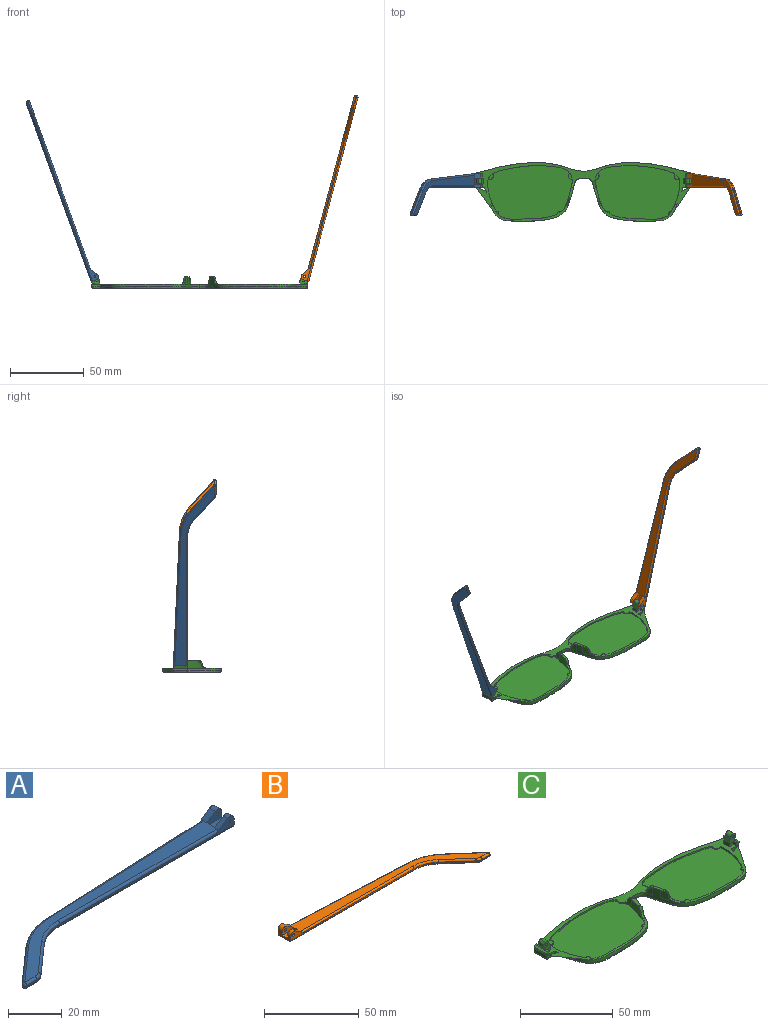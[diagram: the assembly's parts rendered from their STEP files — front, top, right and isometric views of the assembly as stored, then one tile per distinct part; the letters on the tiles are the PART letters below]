
ASSEMBLY  parts=3 mates=2
PART A: 43 faces, bbox 130.2x29.5x5.9 mm
  f0: plane 9.62x3.72mm, normal (1,0,0), area 24.7mm2, adj f1,f3,f4,f5,f10,f16,f18,f28
  f1: cylinder r=2.2mm len=3.45mm, axis (0,-1,0), area 11mm2, adj f0,f2,f4,f37
  f2: plane 6.01x3.91mm, normal (-0.55,0,0.84), area 12.7mm2, adj f1,f4,f9,f19,f37
  f3: plane 2.26x0.1mm, normal (0,0,1), area 0.1mm2, adj f0,f5,f18
  f4: plane 92.1x4.9mm, normal (0,-1,0), area 79.9mm2, adj f0,f1,f2,f14,f19,f36,f42
  f5: plane 93.42x4.13mm, normal (-0.04,1,0), area 64.8mm2, adj f0,f3,f11,f15,f17,f27,f28
  f6: plane 17.82x15.72mm, normal (-0.66,0.75,0), area 14.3mm2, adj f11,f12,f25,f30
  f7: plane 5.46x0.6mm, normal (0,-1,0), area 3.3mm2, adj f12,f13,f23,f32
  f8: plane 14.99x13.23mm, normal (0.66,-0.75,0), area 12mm2, adj f13,f14,f21,f34
  f9: plane 121.18x26.73mm, normal (0,0,1), area 627.7mm2, adj f2,f17,f19,f20,f21,f22,f23,f25
  f10: plane 129.1x27.08mm, normal (0,0,-1), area 686.5mm2, adj f0,f28,f29,f30,f32,f33,f34,f35
  f11: cylinder r=30mm len=18.52mm, axis (0,0,-1), area 12.2mm2, adj f5,f6,f26,f29
  f12: cylinder r=1mm len=1.75mm, axis (0,0,-1), area 1.5mm2, adj f6,f7,f24,f31
  f13: cylinder r=5mm len=3.31mm, axis (0,0,-1), area 2.2mm2, adj f7,f8,f22,f33
  f14: cylinder r=20mm len=13.23mm, axis (0,0,1), area 8.7mm2, adj f4,f8,f20,f35
  f15: plane 5.66x0.25mm, normal (0,0,-1), area 0.7mm2, adj f5,f17,f18
  f16: cylinder r=2.2mm len=3.45mm, axis (0,-1,0), area 14.8mm2, adj f0,f17,f18,f38
  f17: plane 6.01x3.91mm, normal (-0.55,0,0.84), area 16.9mm2, adj f5,f9,f15,f16,f18,f27,f38
  f18: plane 7.92x3.3mm, normal (0,1,0), area 15.9mm2, adj f0,f3,f15,f16,f17,f41
  f19: cylinder r=1mm len=84.18mm, axis (-1,0,0), area 131.4mm2, adj f2,f4,f9,f20
  f20: torus R=21mm, axis (0,0,1), area 23.1mm2, adj f9,f14,f19,f21
  f21: cylinder r=1mm len=15.65mm, axis (-0.75,-0.66,0), area 31.4mm2, adj f8,f9,f20,f22
  f22: torus R=4mm, axis (0,0,1), area 5.3mm2, adj f9,f13,f21,f23
  f23: cylinder r=1mm len=5.46mm, axis (-1,0,0), area 8.6mm2, adj f7,f9,f22,f24
  f24: sphere r=1mm, area 2.4mm2, adj f12,f23,f25
  f25: cylinder r=1mm len=18.48mm, axis (0.75,0.66,0), area 37.3mm2, adj f6,f9,f24,f26
  f26: torus R=29mm, axis (0,0,1), area 31.6mm2, adj f9,f11,f25,f27
  f27: cylinder r=1mm len=85.5mm, axis (1,0.04,0), area 133.5mm2, adj f5,f9,f17,f26
  f28: cylinder r=1mm len=93.46mm, axis (-1,-0.04,0), area 146.9mm2, adj f0,f5,f10,f29
  f29: torus R=29mm, axis (0,0,1), area 31.6mm2, adj f10,f11,f28,f30
  f30: cylinder r=1mm len=18.48mm, axis (-0.75,-0.66,0), area 37.3mm2, adj f6,f10,f29,f31
  f31: sphere r=1mm, area 2.4mm2, adj f12,f30,f32
  f32: cylinder r=1mm len=5.46mm, axis (1,0,0), area 8.6mm2, adj f7,f10,f31,f33
  f33: torus R=4mm, axis (0,0,1), area 5.3mm2, adj f10,f13,f32,f34
  f34: cylinder r=1mm len=15.65mm, axis (0.75,0.66,0), area 31.4mm2, adj f8,f10,f33,f35
  f35: torus R=21mm, axis (0,0,1), area 23.1mm2, adj f10,f14,f34,f36
  f36: cylinder r=1mm len=92.1mm, axis (1,0,0), area 144.7mm2, adj f0,f4,f10,f35
  f37: plane 7.92x4.7mm, normal (0,1,0), area 27mm2, adj f0,f1,f2,f39,f40,f42
  f38: plane 7.92x4.7mm, normal (0,-1,0), area 27mm2, adj f0,f16,f17,f39,f40,f41
  f39: plane 7.92x4.1mm, normal (0,0,1), area 32.5mm2, adj f0,f37,f38,f40
  f40: plane 4.1x1.4mm, normal (1,0,0), area 5.7mm2, adj f9,f37,f38,f39
  f41: cylinder r=0.5mm len=3.1mm, axis (0,-1,0), area 9.7mm2, adj f18,f38
  f42: cylinder r=0.5mm len=2.3mm, axis (0,-1,0), area 7.2mm2, adj f4,f37
PART B: 43 faces, bbox 130.2x29.5x5.9 mm
  f0: plane 9.62x3.72mm, normal (-1,0,0), area 24.7mm2, adj f1,f3,f4,f5,f10,f16,f18,f28
  f1: cylinder r=2.2mm len=3.45mm, axis (0,-1,0), area 11mm2, adj f0,f2,f4,f37
  f2: plane 6.01x3.91mm, normal (0.55,0,0.84), area 12.7mm2, adj f1,f4,f9,f19,f37
  f3: plane 2.26x0.1mm, normal (0,0,1), area 0.1mm2, adj f0,f5,f18
  f4: plane 92.1x4.9mm, normal (0,-1,0), area 78.2mm2, adj f0,f1,f2,f14,f19,f36,f42
  f5: plane 93.42x4.13mm, normal (0.04,1,0), area 64.8mm2, adj f0,f3,f11,f15,f17,f27,f28
  f6: plane 17.82x15.72mm, normal (0.66,0.75,0), area 14.3mm2, adj f11,f12,f25,f30
  f7: plane 5.46x0.6mm, normal (0,-1,0), area 3.3mm2, adj f12,f13,f23,f32
  f8: plane 14.99x13.23mm, normal (-0.66,-0.75,0), area 12mm2, adj f13,f14,f21,f34
  f9: plane 121.18x26.73mm, normal (0,0,1), area 627.7mm2, adj f2,f17,f19,f20,f21,f22,f23,f25
  f10: plane 129.1x27.08mm, normal (0,0,-1), area 686.5mm2, adj f0,f28,f29,f30,f32,f33,f34,f35
  f11: cylinder r=30mm len=18.52mm, axis (0,0,-1), area 12.2mm2, adj f5,f6,f26,f29
  f12: cylinder r=1mm len=1.75mm, axis (0,0,-1), area 1.5mm2, adj f6,f7,f24,f31
  f13: cylinder r=5mm len=3.31mm, axis (0,0,-1), area 2.2mm2, adj f7,f8,f22,f33
  f14: cylinder r=20mm len=13.23mm, axis (0,0,1), area 8.7mm2, adj f4,f8,f20,f35
  f15: plane 5.66x0.25mm, normal (0,0,-1), area 0.7mm2, adj f5,f17,f18
  f16: cylinder r=2.2mm len=3.45mm, axis (0,-1,0), area 14.8mm2, adj f0,f17,f18,f38
  f17: plane 6.01x3.91mm, normal (0.55,0,0.84), area 16.9mm2, adj f5,f9,f15,f16,f18,f27,f38
  f18: plane 7.92x3.3mm, normal (0,1,0), area 14.3mm2, adj f0,f3,f15,f16,f17,f41
  f19: cylinder r=1mm len=84.18mm, axis (1,0,0), area 131.4mm2, adj f2,f4,f9,f20
  f20: torus R=21mm, axis (0,0,1), area 23.1mm2, adj f9,f14,f19,f21
  f21: cylinder r=1mm len=15.65mm, axis (0.75,-0.66,0), area 31.4mm2, adj f8,f9,f20,f22
  f22: torus R=4mm, axis (0,0,1), area 5.3mm2, adj f9,f13,f21,f23
  f23: cylinder r=1mm len=5.46mm, axis (1,0,0), area 8.6mm2, adj f7,f9,f22,f24
  f24: sphere r=1mm, area 2.4mm2, adj f12,f23,f25
  f25: cylinder r=1mm len=18.48mm, axis (-0.75,0.66,0), area 37.3mm2, adj f6,f9,f24,f26
  f26: torus R=29mm, axis (0,0,1), area 31.6mm2, adj f9,f11,f25,f27
  f27: cylinder r=1mm len=85.5mm, axis (-1,0.04,0), area 133.5mm2, adj f5,f9,f17,f26
  f28: cylinder r=1mm len=93.46mm, axis (1,-0.04,0), area 146.9mm2, adj f0,f5,f10,f29
  f29: torus R=29mm, axis (0,0,1), area 31.6mm2, adj f10,f11,f28,f30
  f30: cylinder r=1mm len=18.48mm, axis (0.75,-0.66,0), area 37.3mm2, adj f6,f10,f29,f31
  f31: sphere r=1mm, area 2.4mm2, adj f12,f30,f32
  f32: cylinder r=1mm len=5.46mm, axis (-1,0,0), area 8.6mm2, adj f7,f10,f31,f33
  f33: torus R=4mm, axis (0,0,1), area 5.3mm2, adj f10,f13,f32,f34
  f34: cylinder r=1mm len=15.65mm, axis (-0.75,0.66,0), area 31.4mm2, adj f8,f10,f33,f35
  f35: torus R=21mm, axis (0,0,1), area 23.1mm2, adj f10,f14,f34,f36
  f36: cylinder r=1mm len=92.1mm, axis (-1,0,0), area 144.7mm2, adj f0,f4,f10,f35
  f37: plane 7.92x4.7mm, normal (0,1,0), area 25.4mm2, adj f0,f1,f2,f39,f40,f42
  f38: plane 7.92x4.7mm, normal (0,-1,0), area 25.4mm2, adj f0,f16,f17,f39,f40,f41
  f39: plane 7.92x4.1mm, normal (0,0,1), area 32.5mm2, adj f0,f37,f38,f40
  f40: plane 4.1x1.4mm, normal (-1,0,0), area 5.7mm2, adj f9,f37,f38,f39
  f41: cylinder r=0.88mm len=3.1mm, axis (0,-1,0), area 17mm2, adj f18,f38
  f42: cylinder r=0.88mm len=2.3mm, axis (0,-1,0), area 12.6mm2, adj f4,f37
PART C: 104 faces, bbox 148.3x41x18.1 mm
  f0: plane 4.6x0.78mm, normal (0,0,1), area 0.1mm2, adj f10,f39
  f1: plane 147.86x40.62mm, normal (0,0,1), area 720.8mm2, adj f3,f4,f5,f6,f7,f10,f20,f23
  f2: plane 4.67x1.52mm, normal (0,0,1), area 0.1mm2, adj f6,f38
  f3: plane 1.23x0.04mm, normal (0,0,1), area 0mm2, adj f1,f6,f22
  f4: plane 6.97x5.07mm, normal (0,1,0), area 22.7mm2, adj f1,f20,f21,f25,f27,f28,f30,f31
  f5: plane 3.2x2.36mm, normal (0,-1,0), area 5.7mm2, adj f1,f20,f26,f29
  f6: extruded ~73.26x39.84mm, area 294.3mm2, adj f1,f2,f3,f7,f11,f13,f14,f15
  f7: extruded ~35.39x5.69mm, area 72.2mm2, adj f1,f6,f18,f59
  f8: plane 144.78x37.85mm, normal (0,0,-1), area 582.4mm2, adj f13,f15,f17,f18,f19,f64,f66,f68
  f9: plane 54.45x34.13mm, normal (0,0,-1), area 1549.9mm2, adj f19
  f10: extruded ~57.29x36.52mm, area 218.9mm2, adj f0,f1,f12,f39,f40,f42,f43,f44
  f11: plane 3.75x1.08mm, normal (0,0,1), area 0.1mm2, adj f6,f37
  f12: plane 57.58x36.73mm, normal (0,0,1), area 1771.7mm2, adj f10
  f13: bspline ~73.27x30.39mm, area 161.7mm2, adj f6,f8,f14,f64
  f14: bspline ~1x1mm, area 0.8mm2, adj f6,f13,f15
  f15: bspline ~8.99x1.23mm, area 12.6mm2, adj f6,f8,f14,f16
  f16: bspline ~1.04x1mm, area 0.7mm2, adj f6,f15,f17
  f17: bspline ~45.86x8.59mm, area 59.8mm2, adj f6,f8,f16,f18
  f18: bspline ~37.01x6.7mm, area 56.6mm2, adj f7,f8,f17,f69
  f19: bspline ~56.23x35.9mm, area 235.3mm2, adj f8,f9
  f20: plane 4x2.36mm, normal (-1,0,0), area 9.5mm2, adj f1,f4,f5,f21
  f21: plane 4x0.02mm, normal (0.34,0,0.94), area 0.1mm2, adj f4,f20,f28
  f22: plane 2.76x2.53mm, normal (0,-1,0), area 3.9mm2, adj f3,f26,f27,f35,f52
  f23: plane 7.67x1.6mm, normal (0.94,0,-0.34), area 13mm2, adj f1,f35,f36,f52
  f24: plane 2.1x1.69mm, normal (0,1,0), area 2.8mm2, adj f1,f25,f27,f36,f52
  f25: plane 3.3x2.1mm, normal (-1,0,0), area 6.9mm2, adj f1,f4,f24,f27
  f26: plane 2.35x2.1mm, normal (-1,0,0), area 4.9mm2, adj f1,f5,f22,f27,f29
  f27: plane 9.65x1.24mm, normal (0,0,1), area 8.2mm2, adj f4,f22,f24,f25,f26,f29,f30,f52
  f28: plane 4x3.31mm, normal (-0.94,0,0.34), area 14.1mm2, adj f4,f21,f29,f32
  f29: plane 5.77x5.06mm, normal (0,-1,0), area 17mm2, adj f5,f26,f27,f28,f30,f31,f32,f33
  f30: plane 4x2.21mm, normal (0.94,0,-0.34), area 9.4mm2, adj f4,f27,f29,f33
  f31: plane 4x0.01mm, normal (0.34,0,0.94), area 0mm2, adj f4,f29,f32,f33
  f32: cylinder r=1.98mm len=4mm, axis (0,1,0), area 12.4mm2, adj f4,f28,f29,f31
  f33: cylinder r=1.98mm len=4mm, axis (0,-1,0), area 12.4mm2, adj f4,f29,f30,f31
  f34: cylinder r=0.88mm len=4mm, axis (0,-1,0), area 22mm2, adj f4,f29
  f35: cone r=1mm half-angle=20deg, axis (0,0,1), area 2.3mm2, adj f1,f22,f23,f52
  f36: cylinder r=1mm len=2.28mm, axis (-0.34,0,-0.94), area 3mm2, adj f1,f23,f24,f52
  f37: extruded ~4.92x3.67mm, area 11.8mm2, adj f6,f11,f41
  f38: extruded ~5x4.64mm, area 23.3mm2, adj f2,f6,f40,f42,f51
  f39: extruded ~5x4.5mm, area 17.5mm2, adj f0,f10,f40,f41
  f40: plane 8.99x2.94mm, normal (0,0,1), area 10.5mm2, adj f6,f10,f38,f39,f41,f42
  f41: bspline ~15.56x15.29mm, area 14.1mm2, adj f1,f6,f37,f39,f40
  f42: bspline ~7.27x7.27mm, area 6.2mm2, adj f10,f38,f40,f51
  f43: plane 4.19x2.6mm, normal (0,0,-1), area 6.8mm2, adj f10,f44
  f44: cylinder r=2.28mm len=4.15mm, axis (0,0,1), area 3mm2, adj f1,f10,f43
  f45: plane 3.78x3.41mm, normal (0,0,-1), area 7.2mm2, adj f10,f46
  f46: cylinder r=2.28mm len=3.76mm, axis (0,0,1), area 3.2mm2, adj f1,f10,f45
  f47: plane 2.35x1.81mm, normal (0,0,-1), area 2.3mm2, adj f10,f48
  f48: cylinder r=1.3mm len=2.35mm, axis (0,0,1), area 1.9mm2, adj f1,f10,f47
  f49: plane 2.19x1.79mm, normal (0,0,-1), area 2mm2, adj f10,f50
  f50: cylinder r=1.3mm len=2.18mm, axis (0,0,1), area 1.7mm2, adj f1,f10,f49
  f51: bspline ~3.71x3.51mm, area 5.7mm2, adj f1,f6,f10,f38,f42
  f52: plane 9.71x1.44mm, normal (0.34,0,0.94), area 13.9mm2, adj f22,f23,f24,f27,f35,f36
  f53: plane 4.6x0.78mm, normal (0,0,1), area 0.1mm2, adj f61,f90
  f54: plane 4.67x1.52mm, normal (0,0,1), area 0.1mm2, adj f58,f89
  f55: plane 1.23x0.04mm, normal (0,0,1), area 0mm2, adj f1,f58,f73
  f56: plane 6.97x5.07mm, normal (0,1,0), area 22.7mm2, adj f1,f71,f72,f76,f78,f79,f81,f82
  f57: plane 3.2x2.36mm, normal (0,-1,0), area 5.7mm2, adj f1,f71,f77,f80
  f58: extruded ~73.26x39.84mm, area 294.3mm2, adj f1,f6,f54,f55,f59,f62,f64,f65
  f59: extruded ~35.39x5.69mm, area 72.2mm2, adj f1,f7,f58,f69
  f60: plane 54.45x34.13mm, normal (0,0,-1), area 1549.9mm2, adj f70
  f61: extruded ~57.29x36.52mm, area 219mm2, adj f1,f53,f63,f90,f91,f93,f94,f95
  f62: plane 3.75x1.08mm, normal (0,0,1), area 0.1mm2, adj f58,f88
  f63: plane 57.58x36.73mm, normal (0,0,1), area 1771.7mm2, adj f61
  f64: bspline ~73.83x30.39mm, area 161.7mm2, adj f8,f13,f58,f65
  f65: bspline ~1x1mm, area 0.8mm2, adj f58,f64,f66
  f66: bspline ~8.99x1.23mm, area 12.6mm2, adj f8,f58,f65,f67
  f67: bspline ~1.04x1mm, area 0.8mm2, adj f58,f66,f68
  f68: bspline ~45.86x8.59mm, area 59.8mm2, adj f8,f58,f67,f69
  f69: bspline ~37.01x6.7mm, area 56.6mm2, adj f8,f18,f59,f68
  f70: bspline ~56.22x35.9mm, area 235.3mm2, adj f8,f60
  f71: plane 4x2.36mm, normal (1,0,0), area 9.5mm2, adj f1,f56,f57,f72
  f72: plane 4x0.02mm, normal (-0.34,0,0.94), area 0.1mm2, adj f56,f71,f79
  f73: plane 2.76x2.53mm, normal (0,-1,0), area 3.9mm2, adj f55,f77,f78,f86,f103
  f74: plane 7.67x1.6mm, normal (-0.94,0,-0.34), area 13mm2, adj f1,f86,f87,f103
  f75: plane 2.1x1.69mm, normal (0,1,0), area 2.8mm2, adj f1,f76,f78,f87,f103
  f76: plane 3.3x2.1mm, normal (1,0,0), area 6.9mm2, adj f1,f56,f75,f78
  f77: plane 2.35x2.1mm, normal (1,0,0), area 4.9mm2, adj f1,f57,f73,f78,f80
  f78: plane 9.65x1.24mm, normal (0,0,1), area 8.2mm2, adj f56,f73,f75,f76,f77,f80,f81,f103
  f79: plane 4x3.31mm, normal (0.94,0,0.34), area 14.1mm2, adj f56,f72,f80,f83
  f80: plane 5.77x5.06mm, normal (0,-1,0), area 17mm2, adj f57,f77,f78,f79,f81,f82,f83,f84
  f81: plane 4x2.21mm, normal (-0.94,0,-0.34), area 9.4mm2, adj f56,f78,f80,f84
  f82: plane 4x0.01mm, normal (-0.34,0,0.94), area 0mm2, adj f56,f80,f83,f84
  f83: cylinder r=1.98mm len=4mm, axis (0,1,0), area 12.4mm2, adj f56,f79,f80,f82
  f84: cylinder r=1.98mm len=4mm, axis (0,-1,0), area 12.4mm2, adj f56,f80,f81,f82
  f85: cylinder r=0.88mm len=4mm, axis (0,-1,0), area 22mm2, adj f56,f80
  f86: cone r=1mm half-angle=20deg, axis (0,0,1), area 2.3mm2, adj f1,f73,f74,f103
  f87: cylinder r=1mm len=2.28mm, axis (0.34,0,-0.94), area 3mm2, adj f1,f74,f75,f103
  f88: extruded ~4.92x3.67mm, area 11.8mm2, adj f58,f62,f92
  f89: extruded ~5x4.64mm, area 23.3mm2, adj f54,f58,f91,f93,f102
  f90: extruded ~5x4.5mm, area 17.5mm2, adj f53,f61,f91,f92
  f91: plane 8.99x2.94mm, normal (0,0,1), area 10.5mm2, adj f58,f61,f89,f90,f92,f93
  f92: bspline ~15.56x15.29mm, area 14.1mm2, adj f1,f58,f88,f90,f91
  f93: bspline ~7.27x7.27mm, area 6.2mm2, adj f61,f89,f91,f102
  f94: plane 4.19x2.6mm, normal (0,0,-1), area 6.8mm2, adj f61,f95
  f95: cylinder r=2.28mm len=4.15mm, axis (0,0,1), area 3mm2, adj f1,f61,f94
  f96: plane 3.78x3.41mm, normal (0,0,-1), area 7.2mm2, adj f61,f97
  f97: cylinder r=2.28mm len=3.76mm, axis (0,0,1), area 3.2mm2, adj f1,f61,f96
  f98: plane 2.35x1.81mm, normal (0,0,-1), area 2.3mm2, adj f61,f99
  f99: cylinder r=1.3mm len=2.35mm, axis (0,0,1), area 1.9mm2, adj f1,f61,f98
  f100: plane 2.19x1.79mm, normal (0,0,-1), area 2mm2, adj f61,f101
  f101: cylinder r=1.3mm len=2.18mm, axis (0,0,1), area 1.7mm2, adj f1,f61,f100
  f102: bspline ~3.71x3.51mm, area 5.7mm2, adj f1,f58,f61,f89,f93
  f103: plane 9.71x1.44mm, normal (-0.34,0,0.94), area 13.9mm2, adj f73,f74,f75,f78,f86,f87
PLACE A rot(axis=(0,1,0),70deg) t=(-84.77,-5.75,56)mm
PLACE B rot(axis=(0,-1,0),75deg) t=(68.2,-5.75,-61.61)mm
PLACE C t=(10.15,-1.13,-5.77)mm
MATE revolute A.f1 <-> C.f83  axis (0,-1,0) through (-60.89,2.72,1.22)mm
MATE revolute B.f41 <-> C.f33  axis (0,-1,0) through (81.2,2.72,1.21)mm
